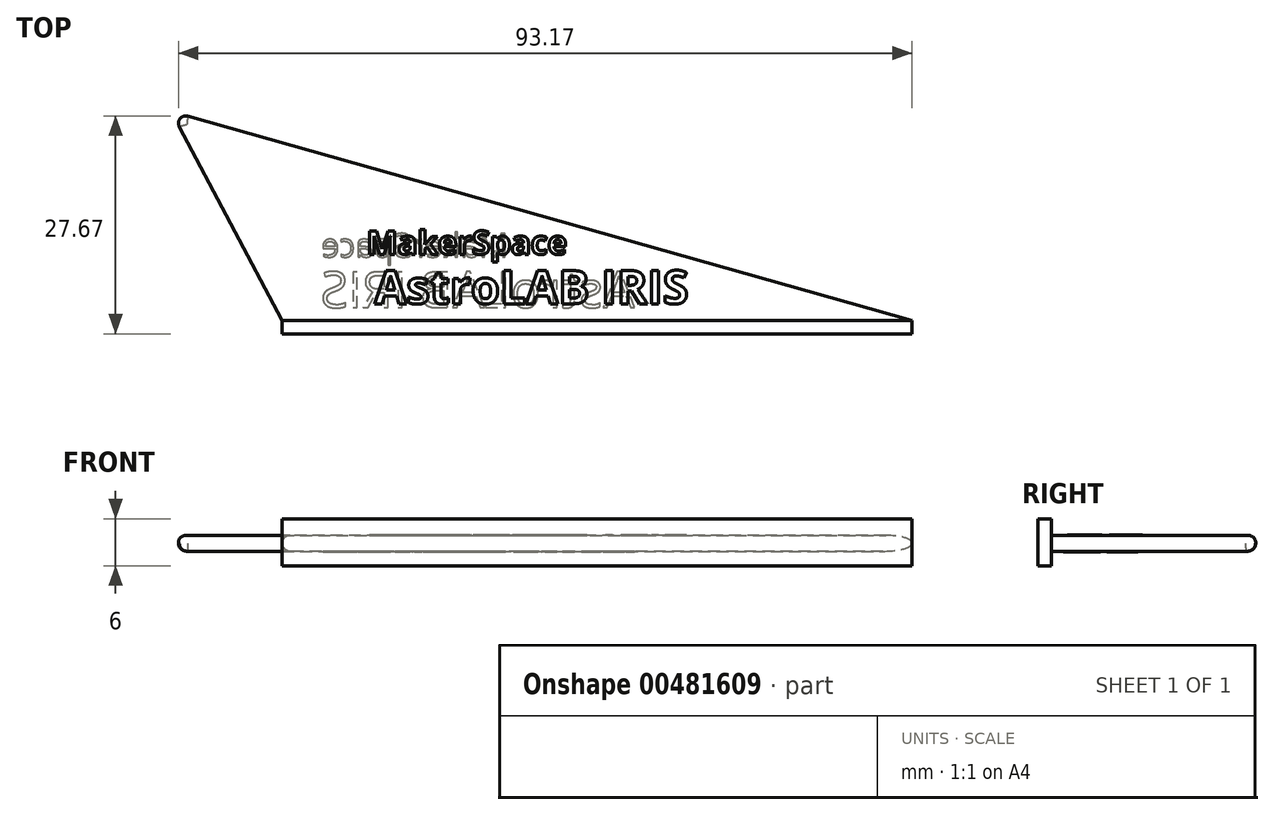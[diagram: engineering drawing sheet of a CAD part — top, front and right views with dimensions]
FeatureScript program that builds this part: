
annotation { "Feature Type Name" : "Feature", "Feature Type Description" : "" }
export const myFeature = defineFeature(function(context is Context, id is Id, definition is map)
    precondition{}
    {
        {
            var Q0;
            Q0=qCreatedBy(makeId("Front.planeOp"),FACE);
            var sketch = newSketch(context, id + "F0", { "sketchPlane" : qUnion([Q0])});
            skLineSegment(sketch, "E0.bottom", {"start": v(49.28, -2.87) * mm, "end": v(-30.72, -2.87) * mm});
            skLineSegment(sketch, "E0.top", {"start": v(49.28, 3.13) * mm, "end": v(-30.72, 3.13) * mm});
            skLineSegment(sketch, "E0.left", {"start": v(49.28, -2.87) * mm, "end": v(49.28, 3.13) * mm});
            skLineSegment(sketch, "E0.right", {"start": v(-30.72, -2.87) * mm, "end": v(-30.72, 3.13) * mm});
            skSolve(sketch);
        }
        {
            var Q0;
            Q0=qCreatedBy(makeId("Top.planeOp"),FACE);
            var sketch = newSketch(context, id + "F1", { "sketchPlane" : qUnion([Q0])});
            skLineSegment(sketch, "E1", {"start": v(-30.72, 0) * mm, "end": v(-44.77, 26.5) * mm});
            skLineSegment(sketch, "E2", {"start": v(-44.77, 26.5) * mm, "end": v(49.28, 0) * mm});
            skLineSegment(sketch, "E3", {"start": v(49.28, 0) * mm, "end": v(-30.72, 0) * mm});
            skSolve(sketch);
        }
        {
            var Q0;
            Q0=makeQuery(id+"F0.imprint","IMPRINT",FACE,{"disambiguationData":[TD([[makeQuery(id+"F0.imprint","IMPRINT",EDGE,{"derivedFrom":sQuery(id+"F0.wireOp",EDGE,"E0.bottom")}),-1.0]])]});
            extrude(context, id + "F2", {"entities" : qUnion([Q0]), "depth" : 1.7 * mm});
        }
        {
            var Q0;
            Q0=makeQuery(id+"F1.imprint","IMPRINT",FACE,{"disambiguationData":[TD([[makeQuery(id+"F1.imprint","IMPRINT",EDGE,{"derivedFrom":sQuery(id+"F1.wireOp",EDGE,"E1")}),-1.0]])]});
            extrude(context, id + "F3", {"entities" : qUnion([Q0]), "operationType" : NewBodyOperationType.ADD, "oppositeDirection" : true, "depth" : 1 * mm});
        }
        {
            var Q0;
            Q0=makeQuery(id+"F3.opExtrude","CAP_FACE",FACE,{"disambiguationData":[OSD([sQuery(id+"F1.wireOp",EDGE,"E1"),sQuery(id+"F1.wireOp",EDGE,"E2"),sQuery(id+"F1.wireOp",EDGE,"E3")])],"isStart":true});
            extrude(context, id + "F4", {"entities" : qUnion([Q0]), "operationType" : NewBodyOperationType.ADD, "depth" : 1 * mm});
        }
        {
            var Q0;
            Q0=makeQuery(id+"F3.opExtrude","CAP_EDGE",EDGE,{"disambiguationData":[OSD([sQuery(id+"F1.wireOp",EDGE,"E1")])],"isStart":false});
            var Q1;
            Q1=makeQuery(id+"F3.opExtrude","CAP_EDGE",EDGE,{"disambiguationData":[OSD([sQuery(id+"F1.wireOp",EDGE,"E2")])],"isStart":false});
            fillet(context, id + "F5", {"entities" : qUnion([Q0, Q1]), "radius" : 1 * mm, "tangentPropagation" : true, "allowEdgeOverflow" : false});
        }
        {
            var Q0;
            Q0=makeQuery(id+"F4.opExtrude","CAP_EDGE",EDGE,{"disambiguationData":[OSD([sQuery(id+"F1.wireOp",EDGE,"E2")])],"isStart":false});
            var Q1;
            {var subQ0=sQuery(id+"F1.wireOp",EDGE,"E2");var subQ1=sQuery(id+"F1.wireOp",EDGE,"E1");Q1=makeQuery(id+"F4.boolean.opBoolean","MERGE",EDGE,{"derivedFrom":[makeQuery(id+"F3.opExtrude","SWEPT_EDGE",EDGE,{"disambiguationData":[OSD([subQ1,subQ0])]}),makeQuery(id+"F4.opExtrude","SWEPT_EDGE",EDGE,{"disambiguationData":[OSD([subQ1,subQ0])]})]});}
            var Q2;
            Q2=makeQuery(id+"F4.opExtrude","CAP_EDGE",EDGE,{"disambiguationData":[OSD([sQuery(id+"F1.wireOp",EDGE,"E1")])],"isStart":false});
            fillet(context, id + "F6", {"entities" : qUnion([Q0, Q1, Q2]), "radius" : 0.9 * mm, "tangentPropagation" : true, "allowEdgeOverflow" : false});
        }
        {
            var Q0;
            Q0=qCreatedBy(makeId("Top.planeOp"),FACE);
            var sketch = newSketch(context, id + "F7", { "sketchPlane" : qUnion([Q0])});
            skText(sketch, "E4", { "text": "AstroLAB IRIS", "fontName": "OpenSans-Bold.ttf"});
            const initialGuessF7  = {"E4": [-0.01898, 0.00211, 1, 0, 0.00425]};
            skSetInitialGuess(sketch, initialGuessF7);
            skSolve(sketch);
        }
        {
            var Q0;
            Q0=qSketchRegion(id+"F7",true);
            extrude(context, id + "F8", {"entities" : qUnion([Q0]), "operationType" : NewBodyOperationType.ADD, "depth" : 1.1 * mm});
        }
        {
            var Q0;
            {var subQ0=sQuery(id+"F1.wireOp",EDGE,"E2");var subQ1=sQuery(id+"F1.wireOp",EDGE,"E1");Q0=makeQuery(id+"F8.boolean.opBoolean","SPLIT",FACE,{"disambiguationData":[TD([makeQuery(id+"F6.opFillet","BLEND_FACE",FACE,{"disambiguationData":[OSD([subQ1])]})])],"derivedFrom":makeQuery(id+"F4.opExtrude","CAP_FACE",FACE,{"disambiguationData":[OSD([subQ1,subQ0,sQuery(id+"F1.wireOp",EDGE,"E3")])],"isStart":false})});}
            var sketch = newSketch(context, id + "F9", { "sketchPlane" : qUnion([Q0])});
            skText(sketch, "E5", { "text": "MakerSpace", "fontName": "OpenSans-Bold.ttf"});
            const initialGuessF9  = {"E5": [-0.01997, 0.00839, 1, 0, 0.003]};
            skSetInitialGuess(sketch, initialGuessF9);
            skSolve(sketch);
        }
        {
            var Q0;
            Q0=qSketchRegion(id+"F9",true);
            extrude(context, id + "F10", {"entities" : qUnion([Q0]), "operationType" : NewBodyOperationType.ADD, "depth" : 0.1 * mm});
        }
        {
            var Q0;
            Q0=makeQuery(id+"F3.opExtrude","CAP_FACE",FACE,{"disambiguationData":[OSD([sQuery(id+"F1.wireOp",EDGE,"E1"),sQuery(id+"F1.wireOp",EDGE,"E2"),sQuery(id+"F1.wireOp",EDGE,"E3")])],"isStart":false});
            var sketch = newSketch(context, id + "F11", { "sketchPlane" : qUnion([Q0])});
            skText(sketch, "E6", { "text": "AstroLAB IRIS", "fontName": "OpenSans-Regular.ttf"});
            skLineSegment(sketch, "E7", {"start": v(32.8, 3.03) * mm, "end": v(-39.17, 3.03) * mm});
            skText(sketch, "E8", { "text": "MakerSpace", "fontName": "OpenSans-Regular.ttf"});
            const initialGuessF11  = {"E6": [0.01406, -0.00162, -1, 0, 0.00459], "E8": [-0.00198, -0.00805, -1, 0, 0.003]};
            skSetInitialGuess(sketch, initialGuessF11);
            skSolve(sketch);
        }
        {
            var Q0;
            Q0 = qSketchRegion(id + "F11", true);
            extrude(context, id + "F12", {"entities" : qUnion([Q0]), "operationType" : NewBodyOperationType.ADD, "depth" : 0.1 * mm});
        }
    });
